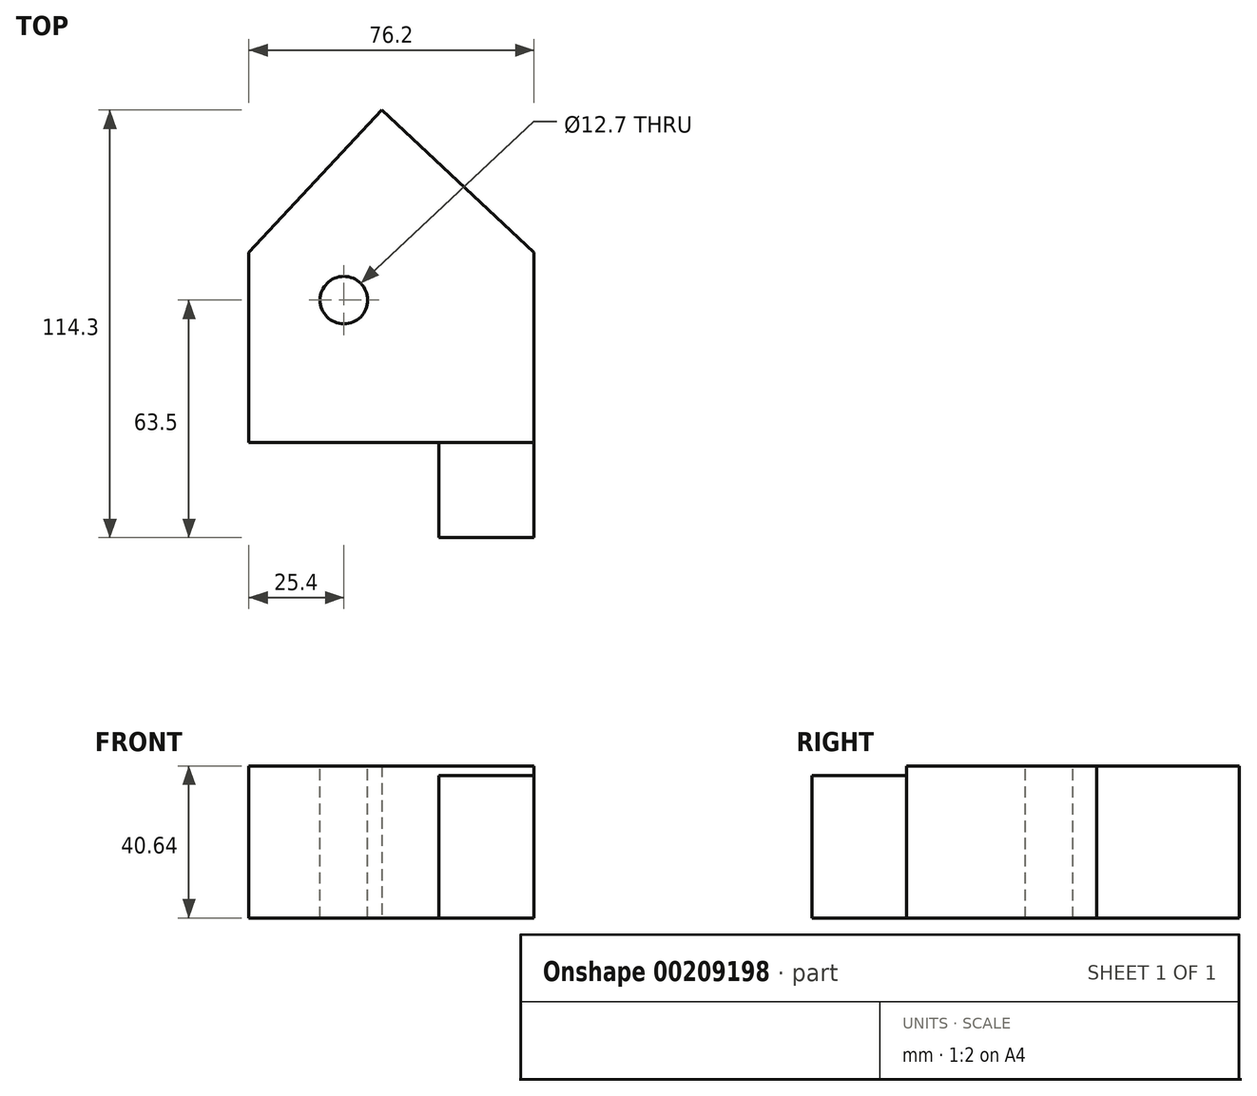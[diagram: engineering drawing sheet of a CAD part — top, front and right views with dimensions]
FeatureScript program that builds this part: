
annotation { "Feature Type Name" : "Feature", "Feature Type Description" : "" }
export const myFeature = defineFeature(function(context is Context, id is Id, definition is map)
    precondition{}
    {
        {
            var Q0;
            Q0=qCreatedBy(makeId("Top.planeOp"),FACE);
            var sketch = newSketch(context, id + "F0", { "sketchPlane" : qUnion([Q0])});
            skLineSegment(sketch, "E0.bottom", {"start": v(0, 0) * mm, "end": v(76.2, 0) * mm});
            skLineSegment(sketch, "E0.top", {"start": v(0, 50.8) * mm, "end": v(76.2, 50.8) * mm});
            skLineSegment(sketch, "E0.left", {"start": v(0, 0) * mm, "end": v(0, 50.8) * mm});
            skLineSegment(sketch, "E0.right", {"start": v(76.2, 0) * mm, "end": v(76.2, 50.8) * mm});
            skLineSegment(sketch, "E1", {"start": v(0, 50.8) * mm, "end": v(35.56, 88.9) * mm});
            skLineSegment(sketch, "E2", {"start": v(35.56, 88.9) * mm, "end": v(76.2, 50.8) * mm});
            skSolve(sketch);
        }
        {
            var Q0;
            Q0 = qSketchRegion(id + "F0", true);
            extrude(context, id + "F1", {"entities" : qUnion([Q0]), "depth" : 40.64 * mm});
        }
        {
            var Q0;
            Q0=makeQuery(id+"F1.opExtrude","CAP_FACE",FACE,{"disambiguationData":[OSD([sQuery(id+"F0.wireOp",EDGE,"E0.bottom"),sQuery(id+"F0.wireOp",EDGE,"E0.left"),sQuery(id+"F0.wireOp",EDGE,"E0.right"),sQuery(id+"F0.wireOp",EDGE,"E1"),sQuery(id+"F0.wireOp",EDGE,"E2")])],"isStart":false});
            var sketch = newSketch(context, id + "F2", { "sketchPlane" : qUnion([Q0])});
            skCircle(sketch, "E3", {"center": v(25.4, 38.1) * mm, "radius": 6.35 * mm});
            skSolve(sketch);
        }
        {
            var Q0;
            Q0 = qSketchRegion(id + "F2", true);
            extrude(context, id + "F3", {"entities" : qUnion([Q0]), "operationType" : NewBodyOperationType.REMOVE, "endBound" : BoundingType.THROUGH_ALL, "oppositeDirection" : true, "depth" : 25.4 * mm});
        }
        {
            var Q0;
            Q0=makeQuery(id+"F1.opExtrude","SWEPT_FACE",FACE,{"disambiguationData":[OSD([sQuery(id+"F0.wireOp",EDGE,"E0.bottom")])]});
            var sketch = newSketch(context, id + "F4", { "sketchPlane" : qUnion([Q0])});
            skLineSegment(sketch, "E4.bottom", {"start": v(76.2, 38.1) * mm, "end": v(50.8, 38.1) * mm});
            skLineSegment(sketch, "E4.top", {"start": v(76.2, 0) * mm, "end": v(50.8, 0) * mm});
            skLineSegment(sketch, "E4.left", {"start": v(76.2, 38.1) * mm, "end": v(76.2, 0) * mm});
            skLineSegment(sketch, "E4.right", {"start": v(50.8, 38.1) * mm, "end": v(50.8, 0) * mm});
            skSolve(sketch);
        }
        {
            var Q0;
            Q0 = qSketchRegion(id + "F4", true);
            extrude(context, id + "F5", {"entities" : qUnion([Q0]), "depth" : 25.4 * mm});
        }
    });
